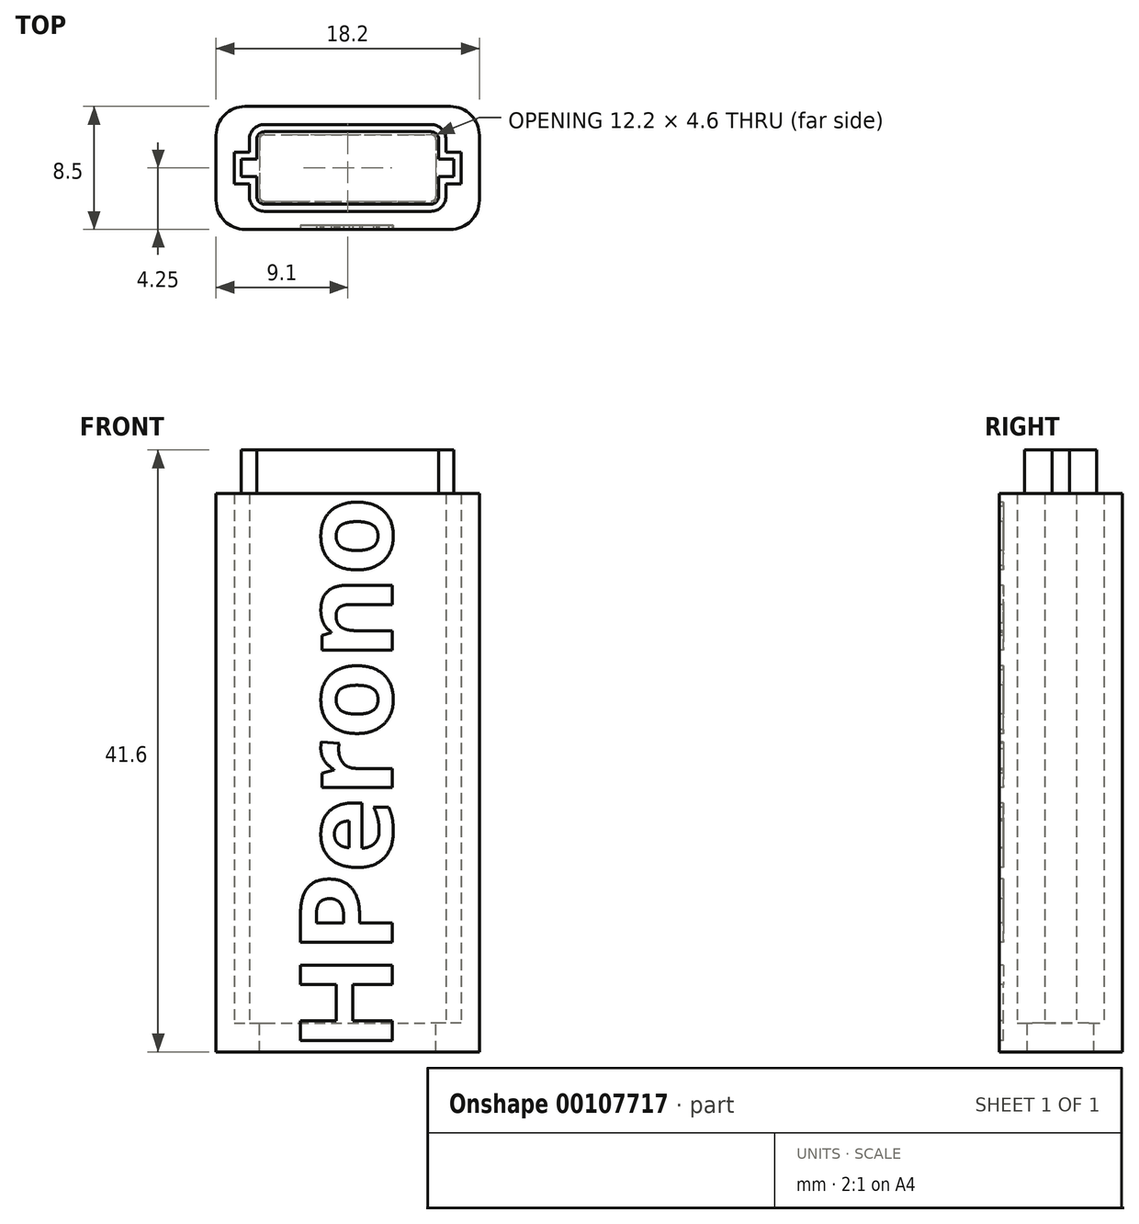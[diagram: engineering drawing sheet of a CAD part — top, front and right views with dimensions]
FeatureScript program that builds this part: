
annotation { "Feature Type Name" : "Feature", "Feature Type Description" : "" }
export const myFeature = defineFeature(function(context is Context, id is Id, definition is map)
    precondition{}
    {
        {
            var Q0;
            Q0=qCreatedBy(makeId("Top.planeOp"),FACE);
            var sketch = newSketch(context, id + "F0", { "sketchPlane" : qUnion([Q0])});
            skLineSegment(sketch, "E0.bottom", {"start": v(-5.75, 2.1) * mm, "end": v(5.75, 2.1) * mm});
            skLineSegment(sketch, "E0.top", {"start": v(-5.75, -2.3) * mm, "end": v(5.75, -2.3) * mm});
            skLineSegment(sketch, "E0.left", {"start": v(-6, 1.85) * mm, "end": v(-6, 0.2) * mm});
            skLineSegment(sketch, "E0.right", {"start": v(6, 1.85) * mm, "end": v(6, 0.2) * mm});
            skPoint(sketch, "E1.visualSharp", {"position": v(-6, 2.1) * mm});
            skArc(sketch, "E1.filletArc", {"start": v(-5.75, 2.1) * mm, "mid": v(-5.93, 2.03) * mm, "end": v(-6, 1.85) * mm});
            skPoint(sketch, "E2.visualSharp", {"position": v(-6, -2.3) * mm});
            skArc(sketch, "E2.filletArc", {"start": v(-6, -2.05) * mm, "mid": v(-5.93, -2.23) * mm, "end": v(-5.75, -2.3) * mm});
            skPoint(sketch, "E3.visualSharp", {"position": v(6, 2.1) * mm});
            skArc(sketch, "E3.filletArc", {"start": v(6, 1.85) * mm, "mid": v(5.93, 2.03) * mm, "end": v(5.75, 2.1) * mm});
            skPoint(sketch, "E4.visualSharp", {"position": v(6, -2.3) * mm});
            skArc(sketch, "E4.filletArc", {"start": v(5.75, -2.3) * mm, "mid": v(5.93, -2.23) * mm, "end": v(6, -2.05) * mm});
            skPoint(sketch, "E5", {"position": v(-6, -0.1) * mm});
            skPoint(sketch, "E6", {"position": v(6, -0.1) * mm});
            skLineSegment(sketch, "E7", {"start": v(-6, -0.1) * mm, "end": v(-7.05, -0.1) * mm});
            skLineSegment(sketch, "E8", {"start": v(6, -0.1) * mm, "end": v(7.05, -0.1) * mm});
            skLineSegment(sketch, "E9", {"start": v(-7.05, -0.1) * mm, "end": v(-7.05, 0.2) * mm});
            skLineSegment(sketch, "E10", {"start": v(-7.05, 0.2) * mm, "end": v(-6, 0.2) * mm});
            skLineSegment(sketch, "E11", {"start": v(-7.05, -0.1) * mm, "end": v(-7.05, -0.4) * mm});
            skLineSegment(sketch, "E12", {"start": v(-7.05, -0.4) * mm, "end": v(-6, -0.4) * mm});
            skLineSegment(sketch, "E13", {"start": v(7.05, -0.1) * mm, "end": v(7.05, -0.4) * mm});
            skLineSegment(sketch, "E14", {"start": v(7.05, -0.4) * mm, "end": v(6, -0.4) * mm});
            skLineSegment(sketch, "E15", {"start": v(7.05, -0.1) * mm, "end": v(7.05, 0.2) * mm});
            skLineSegment(sketch, "E16", {"start": v(7.05, 0.2) * mm, "end": v(6, 0.2) * mm});
            skPoint(sketch, "E17.end.orphan", {"position": v(-7.05, 2.1) * mm});
            skPoint(sketch, "E18.orphan", {"position": v(-7.05, -2.3) * mm});
            skPoint(sketch, "E19.end.orphan", {"position": v(7.05, 2.1) * mm});
            skPoint(sketch, "E20.orphan", {"position": v(7.05, -2.3) * mm});
            skLineSegment(sketch, "E21", {"start": v(-6, 0.2) * mm, "end": v(-6, -0.4) * mm});
            skLineSegment(sketch, "E22", {"start": v(-6, -0.4) * mm, "end": v(-6, -2.05) * mm});
            skLineSegment(sketch, "E23", {"start": v(6, -0.4) * mm, "end": v(6, -2.05) * mm});
            skLineSegment(sketch, "E24", {"start": v(6, 0.2) * mm, "end": v(6, -0.4) * mm});
            skArc(sketch, "E25.0", {"start": v(-5.75, 2.9) * mm, "mid": v(-6.5, 2.6) * mm, "end": v(-6.8, 1.85) * mm});
            skLineSegment(sketch, "E25.1", {"start": v(-5.75, 2.9) * mm, "end": v(5.75, 2.9) * mm});
            skArc(sketch, "E25.2", {"start": v(6.8, 1.85) * mm, "mid": v(6.5, 2.6) * mm, "end": v(5.75, 2.9) * mm});
            skLineSegment(sketch, "E25.3", {"start": v(6.8, 1.85) * mm, "end": v(6.8, 1) * mm});
            skLineSegment(sketch, "E25.4", {"start": v(7.85, 1) * mm, "end": v(6.8, 1) * mm});
            skLineSegment(sketch, "E25.5", {"start": v(-6.8, 1.85) * mm, "end": v(-6.8, 1) * mm});
            skLineSegment(sketch, "E25.6", {"start": v(7.85, 0) * mm, "end": v(7.85, 1) * mm});
            skLineSegment(sketch, "E25.7", {"start": v(7.85, 0) * mm, "end": v(7.85, -1.2) * mm});
            skLineSegment(sketch, "E25.8", {"start": v(-7.85, -1.2) * mm, "end": v(-6.8, -1.2) * mm});
            skLineSegment(sketch, "E25.9", {"start": v(-7.85, 0) * mm, "end": v(-7.85, -1.2) * mm});
            skLineSegment(sketch, "E25.10", {"start": v(-7.85, 0) * mm, "end": v(-7.85, 1) * mm});
            skLineSegment(sketch, "E25.11", {"start": v(-7.85, 1) * mm, "end": v(-6.8, 1) * mm});
            skLineSegment(sketch, "E25.12", {"start": v(-6.8, -1.2) * mm, "end": v(-6.8, -2.05) * mm});
            skArc(sketch, "E25.13", {"start": v(-6.8, -2.05) * mm, "mid": v(-6.5, -2.8) * mm, "end": v(-5.75, -3.1) * mm});
            skLineSegment(sketch, "E25.14", {"start": v(-5.75, -3.1) * mm, "end": v(5.75, -3.1) * mm});
            skArc(sketch, "E25.15", {"start": v(5.75, -3.1) * mm, "mid": v(6.5, -2.8) * mm, "end": v(6.8, -2.05) * mm});
            skLineSegment(sketch, "E25.16", {"start": v(6.8, -1.2) * mm, "end": v(6.8, -2.05) * mm});
            skLineSegment(sketch, "E25.17", {"start": v(7.85, -1.2) * mm, "end": v(6.8, -1.2) * mm});
            skLineSegment(sketch, "E26.0", {"start": v(-7.1, -4.35) * mm, "end": v(7.1, -4.35) * mm});
            skLineSegment(sketch, "E27.0", {"start": v(-7.1, 4.15) * mm, "end": v(7.1, 4.15) * mm});
            skLineSegment(sketch, "E28.0", {"start": v(-9.1, -2.35) * mm, "end": v(-9.1, 2.15) * mm});
            skLineSegment(sketch, "E29.0", {"start": v(9.1, -2.35) * mm, "end": v(9.1, 2.15) * mm});
            skPoint(sketch, "E30.visualSharp", {"position": v(-9.1, 4.15) * mm});
            skArc(sketch, "E30.filletArc", {"start": v(-7.1, 4.15) * mm, "mid": v(-8.51, 3.56) * mm, "end": v(-9.1, 2.15) * mm});
            skPoint(sketch, "E31.visualSharp", {"position": v(-9.1, -4.35) * mm});
            skArc(sketch, "E31.filletArc", {"start": v(-9.1, -2.35) * mm, "mid": v(-8.51, -3.76) * mm, "end": v(-7.1, -4.35) * mm});
            skPoint(sketch, "E32.visualSharp", {"position": v(9.1, -4.35) * mm});
            skArc(sketch, "E32.filletArc", {"start": v(7.1, -4.35) * mm, "mid": v(8.51, -3.76) * mm, "end": v(9.1, -2.35) * mm});
            skPoint(sketch, "E33.visualSharp", {"position": v(9.1, 4.15) * mm});
            skArc(sketch, "E33.filletArc", {"start": v(9.1, 2.15) * mm, "mid": v(8.51, 3.56) * mm, "end": v(7.1, 4.15) * mm});
            skLineSegment(sketch, "E34", {"start": v(-6.8, 1) * mm, "end": v(-6.8, -1.2) * mm});
            skLineSegment(sketch, "E35", {"start": v(6.8, 1) * mm, "end": v(6.8, -1.2) * mm});
            skArc(sketch, "E36.0", {"start": v(-6.1, -2.05) * mm, "mid": v(-6, -2.3) * mm, "end": v(-5.75, -2.4) * mm});
            skLineSegment(sketch, "E36.1", {"start": v(6.1, 1.85) * mm, "end": v(6.1, 0.4) * mm});
            skLineSegment(sketch, "E36.2", {"start": v(6.1, 0.4) * mm, "end": v(6.1, -0.4) * mm});
            skLineSegment(sketch, "E36.3", {"start": v(6.1, -0.4) * mm, "end": v(6.1, -2.05) * mm});
            skArc(sketch, "E36.4", {"start": v(5.75, -2.4) * mm, "mid": v(6, -2.3) * mm, "end": v(6.1, -2.05) * mm});
            skArc(sketch, "E36.5", {"start": v(6.1, 1.85) * mm, "mid": v(6, 2.1) * mm, "end": v(5.75, 2.2) * mm});
            skLineSegment(sketch, "E36.6", {"start": v(-5.75, -2.4) * mm, "end": v(5.75, -2.4) * mm});
            skLineSegment(sketch, "E36.7", {"start": v(-5.75, 2.2) * mm, "end": v(5.75, 2.2) * mm});
            skArc(sketch, "E36.8", {"start": v(-5.75, 2.2) * mm, "mid": v(-6, 2.1) * mm, "end": v(-6.1, 1.85) * mm});
            skLineSegment(sketch, "E36.9", {"start": v(-6.1, 1.85) * mm, "end": v(-6.1, 0.4) * mm});
            skLineSegment(sketch, "E36.10", {"start": v(-6.1, 0.4) * mm, "end": v(-6.1, -0.4) * mm});
            skLineSegment(sketch, "E36.11", {"start": v(-6.1, -0.4) * mm, "end": v(-6.1, -2.05) * mm});
            skSolve(sketch);
        }
        {
            var Q0;
            Q0=makeQuery(id+"F0.imprint","IMPRINT",FACE,{"disambiguationData":[TD([[makeQuery(id+"F0.imprint","IMPRINT",EDGE,{"derivedFrom":sQuery(id+"F0.wireOp",EDGE,"E25.0")}),-1.0]])]});
            extrude(context, id + "F1", {"entities" : qUnion([Q0]), "depth" : 36.6 * mm});
        }
        {
            var Q0;
            {var subQ4=sQuery(id+"F0.wireOp",EDGE,"E9");Q0=makeQuery(id+"F0.imprint","IMPRINT",FACE,{"disambiguationData":[TD([[makeQuery(id+"F0.imprint","IMPRINT",EDGE,{"derivedFrom":subQ4}),1.0]])]});}
            var Q1;
            {var subQ0=sQuery(id+"F0.wireOp",EDGE,"E9");Q1=makeQuery(id+"F0.imprint","IMPRINT",FACE,{"disambiguationData":[TD([[makeQuery(id+"F0.imprint","IMPRINT",EDGE,{"derivedFrom":subQ0}),-1.0]])]});}
            var Q2;
            {var subQ0=sQuery(id+"F0.wireOp",EDGE,"E11");Q2=makeQuery(id+"F0.imprint","IMPRINT",FACE,{"disambiguationData":[TD([[makeQuery(id+"F0.imprint","IMPRINT",EDGE,{"derivedFrom":subQ0}),1.0]])]});}
            var Q3;
            {var subQ0=sQuery(id+"F0.wireOp",EDGE,"E15");Q3=makeQuery(id+"F0.imprint","IMPRINT",FACE,{"disambiguationData":[TD([[makeQuery(id+"F0.imprint","IMPRINT",EDGE,{"derivedFrom":subQ0}),1.0]])]});}
            var Q4;
            {var subQ0=sQuery(id+"F0.wireOp",EDGE,"E13");Q4=makeQuery(id+"F0.imprint","IMPRINT",FACE,{"disambiguationData":[TD([[makeQuery(id+"F0.imprint","IMPRINT",EDGE,{"derivedFrom":subQ0}),-1.0]])]});}
            var Q5;
            {var subQ7=sQuery(id+"F0.wireOp",EDGE,"E13");Q5=makeQuery(id+"F0.imprint","IMPRINT",FACE,{"disambiguationData":[TD([[makeQuery(id+"F0.imprint","IMPRINT",EDGE,{"derivedFrom":subQ7}),1.0]])]});}
            var Q6;
            Q6=makeQuery(id+"F0.imprint","IMPRINT",FACE,{"disambiguationData":[TD([[makeQuery(id+"F0.imprint","IMPRINT",EDGE,{"derivedFrom":sQuery(id+"F0.wireOp",EDGE,"E25.0")}),-1.0]])]});
            var Q7;
            {var subQ1=sQuery(id+"F0.wireOp",EDGE,"E25.12");Q7=makeQuery(id+"F0.imprint","IMPRINT",FACE,{"disambiguationData":[TD([[makeQuery(id+"F0.imprint","IMPRINT",EDGE,{"derivedFrom":subQ1}),1.0]])]});}
            var Q8;
            {var subQ0=sQuery(id+"F0.wireOp",EDGE,"E36.10");var subQ1=sQuery(id+"F0.wireOp",EDGE,"E7");var subQ2=makeQuery(id+"F0.imprint","INTERSECT",VERTEX,{"derivedFrom":[subQ1,subQ0]});Q8=makeQuery(id+"F0.imprint","IMPRINT",FACE,{"disambiguationData":[TD([[makeQuery(id+"F0.imprint","IMPRINT",EDGE,{"disambiguationData":[TD([[subQ2,-1.0]])],"derivedFrom":subQ1}),1.0]])]});}
            var Q9;
            {var subQ0=sQuery(id+"F0.wireOp",EDGE,"E36.10");var subQ1=sQuery(id+"F0.wireOp",EDGE,"E7");var subQ2=makeQuery(id+"F0.imprint","INTERSECT",VERTEX,{"derivedFrom":[subQ1,subQ0]});Q9=makeQuery(id+"F0.imprint","IMPRINT",FACE,{"disambiguationData":[TD([[makeQuery(id+"F0.imprint","IMPRINT",EDGE,{"disambiguationData":[TD([[subQ2,-1.0]])],"derivedFrom":subQ1}),-1.0]])]});}
            var Q10;
            Q10=makeQuery(id+"F0.imprint","IMPRINT",FACE,{"disambiguationData":[TD([[makeQuery(id+"F0.imprint","IMPRINT",EDGE,{"derivedFrom":sQuery(id+"F0.wireOp",EDGE,"E25.0")}),1.0]])]});
            var Q11;
            {var subQ0=sQuery(id+"F0.wireOp",EDGE,"E36.2");var subQ1=sQuery(id+"F0.wireOp",EDGE,"E8");var subQ2=makeQuery(id+"F0.imprint","INTERSECT",VERTEX,{"derivedFrom":[subQ1,subQ0]});Q11=makeQuery(id+"F0.imprint","IMPRINT",FACE,{"disambiguationData":[TD([[makeQuery(id+"F0.imprint","IMPRINT",EDGE,{"disambiguationData":[TD([[subQ2,-1.0]])],"derivedFrom":subQ1}),1.0]])]});}
            var Q12;
            {var subQ0=sQuery(id+"F0.wireOp",EDGE,"E36.2");var subQ1=sQuery(id+"F0.wireOp",EDGE,"E8");var subQ2=makeQuery(id+"F0.imprint","INTERSECT",VERTEX,{"derivedFrom":[subQ1,subQ0]});Q12=makeQuery(id+"F0.imprint","IMPRINT",FACE,{"disambiguationData":[TD([[makeQuery(id+"F0.imprint","IMPRINT",EDGE,{"disambiguationData":[TD([[subQ2,-1.0]])],"derivedFrom":subQ1}),-1.0]])]});}
            extrude(context, id + "F2", {"entities" : qUnion([Q0, Q1, Q2, Q3, Q4, Q5, Q6, Q7, Q8, Q9, Q10, Q11, Q12]), "operationType" : NewBodyOperationType.ADD, "oppositeDirection" : true, "depth" : 2 * mm});
        }
        {
            var Q0;
            {var subQ0=sQuery(id+"F0.wireOp",EDGE,"E26.0");Q0=makeQuery(id+"F2.boolean.opBoolean","MERGE",FACE,{"derivedFrom":[makeQuery(id+"F1.opExtrude","SWEPT_FACE",FACE,{"disambiguationData":[OSD([subQ0])]}),makeQuery(id+"F2.opExtrude","SWEPT_FACE",FACE,{"disambiguationData":[OSD([subQ0])]})]});}
            var sketch = newSketch(context, id + "F3", { "sketchPlane" : qUnion([Q0])});
            skLineSegment(sketch, "E37.1", {"start": v(-7.1, 36.6) * mm, "end": v(7.1, 36.6) * mm});
            skLineSegment(sketch, "E37.2", {"start": v(-7.1, 36.6) * mm, "end": v(-7.1, -2) * mm});
            skLineSegment(sketch, "E37.3", {"start": v(7.1, 36.6) * mm, "end": v(7.1, -2) * mm});
            skLineSegment(sketch, "E37.4", {"start": v(-7.1, -2) * mm, "end": v(7.1, -2) * mm});
            skText(sketch, "E38", { "text": "HPerono", "fontName": "OpenSans-Bold.ttf"});
            const initialGuessF3  = {"E38": [0.00307, -0.002, 0, 1, 0.00638]};
            skSetInitialGuess(sketch, initialGuessF3);
            skSolve(sketch);
        }
        {
            var Q0;
            Q0=makeQuery(id+"F3.imprint","IMPRINT",FACE,{"disambiguationData":[TD([[makeQuery(id+"F3.imprint","IMPRINT",EDGE,{"derivedFrom":sQuery(id+"F3.wireOp",EDGE,"E38.sketch_text.stroke-76")}),-1.0]])]});
            var Q1;
            Q1=makeQuery(id+"F3.imprint","IMPRINT",FACE,{"disambiguationData":[TD([[makeQuery(id+"F3.imprint","IMPRINT",EDGE,{"derivedFrom":sQuery(id+"F3.wireOp",EDGE,"E38.sketch_text.stroke-58")}),-1.0]])]});
            var Q2;
            Q2=makeQuery(id+"F3.imprint","IMPRINT",FACE,{"disambiguationData":[TD([[makeQuery(id+"F3.imprint","IMPRINT",EDGE,{"derivedFrom":sQuery(id+"F3.wireOp",EDGE,"E38.sketch_text.stroke-45")}),-1.0]])]});
            var Q3;
            Q3=makeQuery(id+"F3.imprint","IMPRINT",FACE,{"disambiguationData":[TD([[makeQuery(id+"F3.imprint","IMPRINT",EDGE,{"derivedFrom":sQuery(id+"F3.wireOp",EDGE,"E38.sketch_text.stroke-25")}),-1.0]])]});
            var Q4;
            Q4=makeQuery(id+"F3.imprint","IMPRINT",FACE,{"disambiguationData":[TD([[makeQuery(id+"F3.imprint","IMPRINT",EDGE,{"derivedFrom":sQuery(id+"F3.wireOp",EDGE,"E38.sketch_text.stroke-0")}),-1.0]])]});
            var Q5;
            Q5=makeQuery(id+"F3.imprint","IMPRINT",FACE,{"disambiguationData":[TD([[makeQuery(id+"F3.imprint","IMPRINT",EDGE,{"derivedFrom":sQuery(id+"F3.wireOp",EDGE,"E38.sketch_text.stroke-79")}),-1.0]])]});
            var Q6;
            Q6=makeQuery(id+"F3.imprint","IMPRINT",FACE,{"disambiguationData":[TD([[makeQuery(id+"F3.imprint","IMPRINT",EDGE,{"derivedFrom":sQuery(id+"F3.wireOp",EDGE,"E38.sketch_text.stroke-96")}),-1.0]])]});
            extrude(context, id + "F4", {"entities" : qUnion([Q0, Q1, Q2, Q3, Q4, Q5, Q6]), "operationType" : NewBodyOperationType.REMOVE, "oppositeDirection" : true, "depth" : .3 * mm});
        }
        {
            var Q0;
            Q0=makeQuery(id+"F1.opExtrude","CAP_FACE",FACE,{"disambiguationData":[OSD([sQuery(id+"F0.wireOp",EDGE,"E25.0"),sQuery(id+"F0.wireOp",EDGE,"E25.1"),sQuery(id+"F0.wireOp",EDGE,"E25.2"),sQuery(id+"F0.wireOp",EDGE,"E25.3"),sQuery(id+"F0.wireOp",EDGE,"E25.4"),sQuery(id+"F0.wireOp",EDGE,"E25.5"),sQuery(id+"F0.wireOp",EDGE,"E25.6"),sQuery(id+"F0.wireOp",EDGE,"E25.7"),sQuery(id+"F0.wireOp",EDGE,"E25.8"),sQuery(id+"F0.wireOp",EDGE,"E25.9"),sQuery(id+"F0.wireOp",EDGE,"E25.10"),sQuery(id+"F0.wireOp",EDGE,"E25.11"),sQuery(id+"F0.wireOp",EDGE,"E25.12"),sQuery(id+"F0.wireOp",EDGE,"E25.13"),sQuery(id+"F0.wireOp",EDGE,"E25.14"),sQuery(id+"F0.wireOp",EDGE,"E25.15"),sQuery(id+"F0.wireOp",EDGE,"E25.16"),sQuery(id+"F0.wireOp",EDGE,"E25.17"),sQuery(id+"F0.wireOp",EDGE,"E26.0"),sQuery(id+"F0.wireOp",EDGE,"E27.0"),sQuery(id+"F0.wireOp",EDGE,"E28.0"),sQuery(id+"F0.wireOp",EDGE,"E29.0"),sQuery(id+"F0.wireOp",EDGE,"E30.filletArc"),sQuery(id+"F0.wireOp",EDGE,"E31.filletArc"),sQuery(id+"F0.wireOp",EDGE,"E32.filletArc"),sQuery(id+"F0.wireOp",EDGE,"E33.filletArc")])],"isStart":false});
            var sketch = newSketch(context, id + "F5", { "sketchPlane" : qUnion([Q0])});
            skLineSegment(sketch, "E39.0", {"start": v(7.35, -0.7) * mm, "end": v(6.3, -0.7) * mm});
            skLineSegment(sketch, "E39.1", {"start": v(7.35, -0.7) * mm, "end": v(7.35, 0.5) * mm});
            skLineSegment(sketch, "E39.2", {"start": v(7.35, 0.5) * mm, "end": v(6.3, 0.5) * mm});
            skLineSegment(sketch, "E39.3", {"start": v(6.3, 1.85) * mm, "end": v(6.3, 0.5) * mm});
            skArc(sketch, "E39.4", {"start": v(6.3, 1.85) * mm, "mid": v(6.14, 2.24) * mm, "end": v(5.75, 2.4) * mm});
            skLineSegment(sketch, "E39.5", {"start": v(-6.3, -0.7) * mm, "end": v(-6.3, -2.05) * mm});
            skArc(sketch, "E39.6", {"start": v(-6.3, -2.05) * mm, "mid": v(-6.14, -2.44) * mm, "end": v(-5.75, -2.6) * mm});
            skLineSegment(sketch, "E39.7", {"start": v(-5.75, -2.6) * mm, "end": v(5.75, -2.6) * mm});
            skArc(sketch, "E39.8", {"start": v(5.75, -2.6) * mm, "mid": v(6.14, -2.44) * mm, "end": v(6.3, -2.05) * mm});
            skLineSegment(sketch, "E39.9", {"start": v(-7.35, -0.7) * mm, "end": v(-6.3, -0.7) * mm});
            skLineSegment(sketch, "E39.10", {"start": v(-7.35, 0.5) * mm, "end": v(-7.35, -0.7) * mm});
            skLineSegment(sketch, "E39.11", {"start": v(-7.35, 0.5) * mm, "end": v(-6.3, 0.5) * mm});
            skLineSegment(sketch, "E39.12", {"start": v(-6.3, 1.85) * mm, "end": v(-6.3, 0.5) * mm});
            skArc(sketch, "E39.13", {"start": v(-5.75, 2.4) * mm, "mid": v(-6.14, 2.24) * mm, "end": v(-6.3, 1.85) * mm});
            skLineSegment(sketch, "E39.14", {"start": v(6.3, -0.7) * mm, "end": v(6.3, -2.05) * mm});
            skLineSegment(sketch, "E39.15", {"start": v(-5.75, 2.4) * mm, "end": v(5.75, 2.4) * mm});
            skLineSegment(sketch, "E40", {"start": v(-6.3, -0.7) * mm, "end": v(-6.3, 0.5) * mm});
            skLineSegment(sketch, "E41", {"start": v(6.3, -0.7) * mm, "end": v(6.3, 0.5) * mm});
            skPoint(sketch, "E42", {"position": v(5.75, 2.9) * mm});
            skPoint(sketch, "E43", {"position": v(5.75, -3.1) * mm});
            skSolve(sketch);
        }
        {
            var Q0;
            Q0=qSketchRegion(id+"F5",true);
            extrude(context, id + "F6", {"entities" : qUnion([Q0]), "depth" : 3 * mm});
        }
    });
